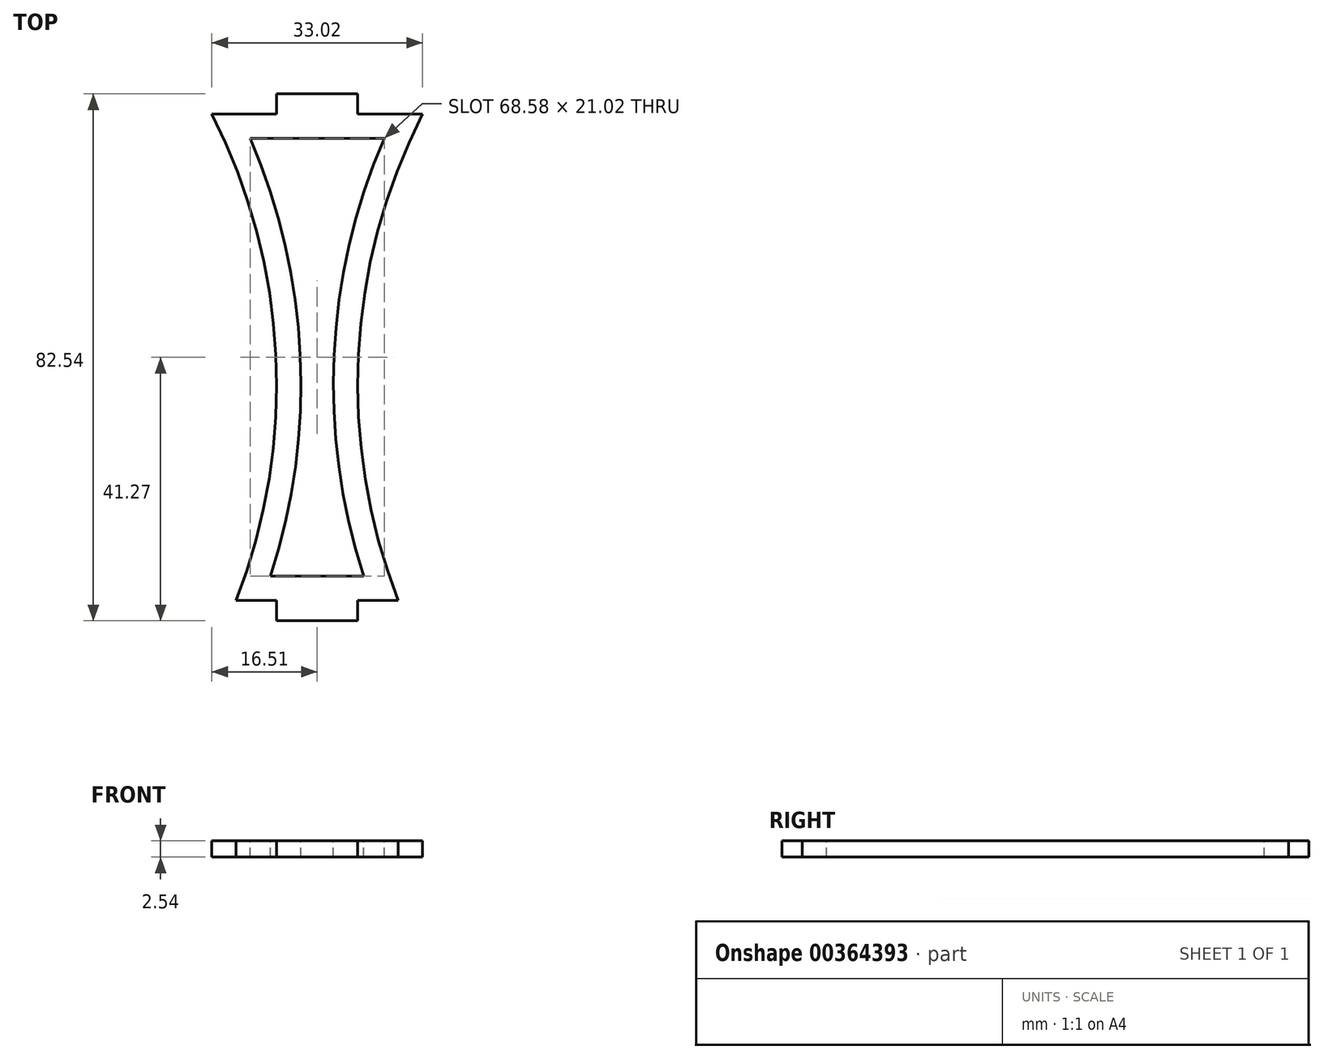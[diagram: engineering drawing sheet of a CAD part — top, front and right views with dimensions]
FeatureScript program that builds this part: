
annotation { "Feature Type Name" : "Feature", "Feature Type Description" : "" }
export const myFeature = defineFeature(function(context is Context, id is Id, definition is map)
    precondition{}
    {
        {
            var Q0;
            Q0=qCreatedBy(makeId("Top.planeOp"),FACE);
            var sketch = newSketch(context, id + "F0", { "sketchPlane" : qUnion([Q0])});
            skLineSegment(sketch, "E0", {"start": v(-12.7, -38.1) * mm, "end": v(-6.35, -38.1) * mm});
            skLineSegment(sketch, "E1", {"start": v(-16.5, 38.1) * mm, "end": v(-6.35, 38.1) * mm});
            skArc(sketch, "E2", {"start": v(-12.7, -38.1) * mm, "mid": v(-6.47, 0.4) * mm, "end": v(-16.5, 38.1) * mm});
            skArc(sketch, "E3.MirrorCS", {"start": v(12.7, -38.1) * mm, "mid": v(6.47, 0.4) * mm, "end": v(16.5, 38.1) * mm});
            skLineSegment(sketch, "E4", {"start": v(-6.35, -38.1) * mm, "end": v(-6.35, -41.27) * mm});
            skLineSegment(sketch, "E5", {"start": v(-6.35, -41.28) * mm, "end": v(6.35, -41.28) * mm});
            skLineSegment(sketch, "E6", {"start": v(6.35, -41.27) * mm, "end": v(6.35, -38.1) * mm});
            skLineSegment(sketch, "E7.trimOffspring", {"start": v(6.35, -38.1) * mm, "end": v(12.7, -38.1) * mm});
            skLineSegment(sketch, "E8", {"start": v(-6.35, 38.1) * mm, "end": v(-6.35, 41.28) * mm});
            skLineSegment(sketch, "E9", {"start": v(-6.35, 41.28) * mm, "end": v(6.35, 41.28) * mm});
            skLineSegment(sketch, "E10", {"start": v(6.35, 41.28) * mm, "end": v(6.35, 38.1) * mm});
            skLineSegment(sketch, "E11.trimOffspring", {"start": v(6.35, 38.1) * mm, "end": v(16.51, 38.1) * mm});
            skSolve(sketch);
        }
        {
            var Q0;
            Q0=makeQuery(id+"F0.imprint","IMPRINT",FACE,{"disambiguationData":[TD([[makeQuery(id+"F0.imprint","IMPRINT",EDGE,{"derivedFrom":sQuery(id+"F0.wireOp",EDGE,"E0")}),1.0]])]});
            extrude(context, id + "F1", {"entities" : qUnion([Q0]), "depth" : 2.54 * mm});
        }
        {
            var Q0;
            Q0=makeQuery(id+"F1.opExtrude","CAP_FACE",FACE,{"disambiguationData":[OSD([sQuery(id+"F0.wireOp",EDGE,"E0"),sQuery(id+"F0.wireOp",EDGE,"E1"),sQuery(id+"F0.wireOp",EDGE,"E2"),sQuery(id+"F0.wireOp",EDGE,"E3.MirrorCS"),sQuery(id+"F0.wireOp",EDGE,"E4"),sQuery(id+"F0.wireOp",EDGE,"E5"),sQuery(id+"F0.wireOp",EDGE,"E6"),sQuery(id+"F0.wireOp",EDGE,"E7.trimOffspring"),sQuery(id+"F0.wireOp",EDGE,"E8"),sQuery(id+"F0.wireOp",EDGE,"E9"),sQuery(id+"F0.wireOp",EDGE,"E10"),sQuery(id+"F0.wireOp",EDGE,"E11.trimOffspring")])],"isStart":false});
            var sketch = newSketch(context, id + "F2", { "sketchPlane" : qUnion([Q0])});
            skArc(sketch, "E12.0", {"start": v(-7.3, -34.3) * mm, "mid": v(-2.65, 0.3) * mm, "end": v(-10.51, 34.3) * mm});
            skArc(sketch, "E13.MirrorCS", {"start": v(7.3, -34.3) * mm, "mid": v(2.65, 0.3) * mm, "end": v(10.51, 34.3) * mm});
            skLineSegment(sketch, "E14", {"start": v(-10.51, 34.3) * mm, "end": v(10.51, 34.3) * mm});
            skLineSegment(sketch, "E15", {"start": v(-7.3, -34.3) * mm, "end": v(7.3, -34.3) * mm});
            skPoint(sketch, "E16.orphan", {"position": v(-13.11, 39.83) * mm});
            skPoint(sketch, "E17.orphan", {"position": v(13.11, 39.83) * mm});
            skPoint(sketch, "E18.orphan", {"position": v(9.15, -39.48) * mm});
            skPoint(sketch, "E19.orphan", {"position": v(-9.15, -39.48) * mm});
            skSolve(sketch);
        }
        {
            var Q0;
            Q0=makeQuery(id+"F2.imprint","IMPRINT",FACE,{"disambiguationData":[TD([[makeQuery(id+"F2.imprint","IMPRINT",EDGE,{"derivedFrom":sQuery(id+"F2.wireOp",EDGE,"E12.0")}),-1.0]])]});
            extrude(context, id + "F3", {"entities" : qUnion([Q0]), "operationType" : NewBodyOperationType.REMOVE, "endBound" : BoundingType.UP_TO_NEXT, "oppositeDirection" : true, "depth" : 25.4 * mm});
        }
    });
